# Revit family: Curtain_Panel_DORMA_Visur
name_source: partatom
category: Fassadenelemente
revit_build: Autodesk Revit 2016 (Build: 20150220_1215(x64)
units: mm (PartAtom-declared; Revit-internal decimal feet)

## family parameters
Beim Laden mit Abzugskörper schneiden = Nein
Gemeinsam genutzt = Nein
Immer vertikal = Ja
OmniClass-Nummer = 23.30.10.00
OmniClass-Titel = Doors

## types (2) — shared parameters
Analytische Konstruktion = <None>
Bauelement = L20
Baugruppenkennzeichen = C1020100
Beschreibung = All-glass double action doors without any visible fixings. Meet VISUR, a system patented for DORMA that secures double-action glass doors without the need for any visually disruptive functional elements. VISUR presents the door in perfect transparency. Rather than cluttering the outline of the leaf, the hardware components are located in the surrounding structures.
Glazing Material = Glass-Dorma Glazing-Clear
Hersteller = DORMA
Ironmongery = Aluminium-Dorma Metal-Anodized Silver
_current revision = 1
zero-valued in all types: Barcode, NominalHeight, NominalWidth, Offset, SerialNumber, TagNumber, WarrentyDuration

## per-type parameters (varying)
| type | BIMobject category | COBIe Type Category | Design country | EAN code | Edition number | IFC Classification | Manufacturer country | Manufacturer name | Material main | Material secondary | Modell | NBS Reference Code | NBS Reference Description | Product SKU | Product name | Thickness | UNSPSC Code | URL | Uniclass 2.0 Code | Weight Net (Kg) |
| 10mm |  |  |  |  |  |  |  |  |  |  | DORMA Visur |  |  |  |  | 10 mm  [stored 0.0328084 ft] |  | http://www.dorma-uk.co.uk |  |  |
| 12mm | Doors | Door | Germany | http://- | 1 | Door | Germany | DORMA | Metal | Glass | DORMA Visur Sidelight | 36-37-21 | Door Hinges | VISUR_001-1 | Glass Swing Door Fittings VISUR | 12 mm  [stored 0.0393701 ft] | 301715 | http://www.dorma.com | PR-36-37-21 | 0 |

note: [stored X ft] marks values corroborated as IEEE doubles in the binary element streams (Revit-internal decimal feet)

## geometry (parser evidence)
native form markers: Blend x4, Sweep x3
no freeform markers — native parametric forms only
